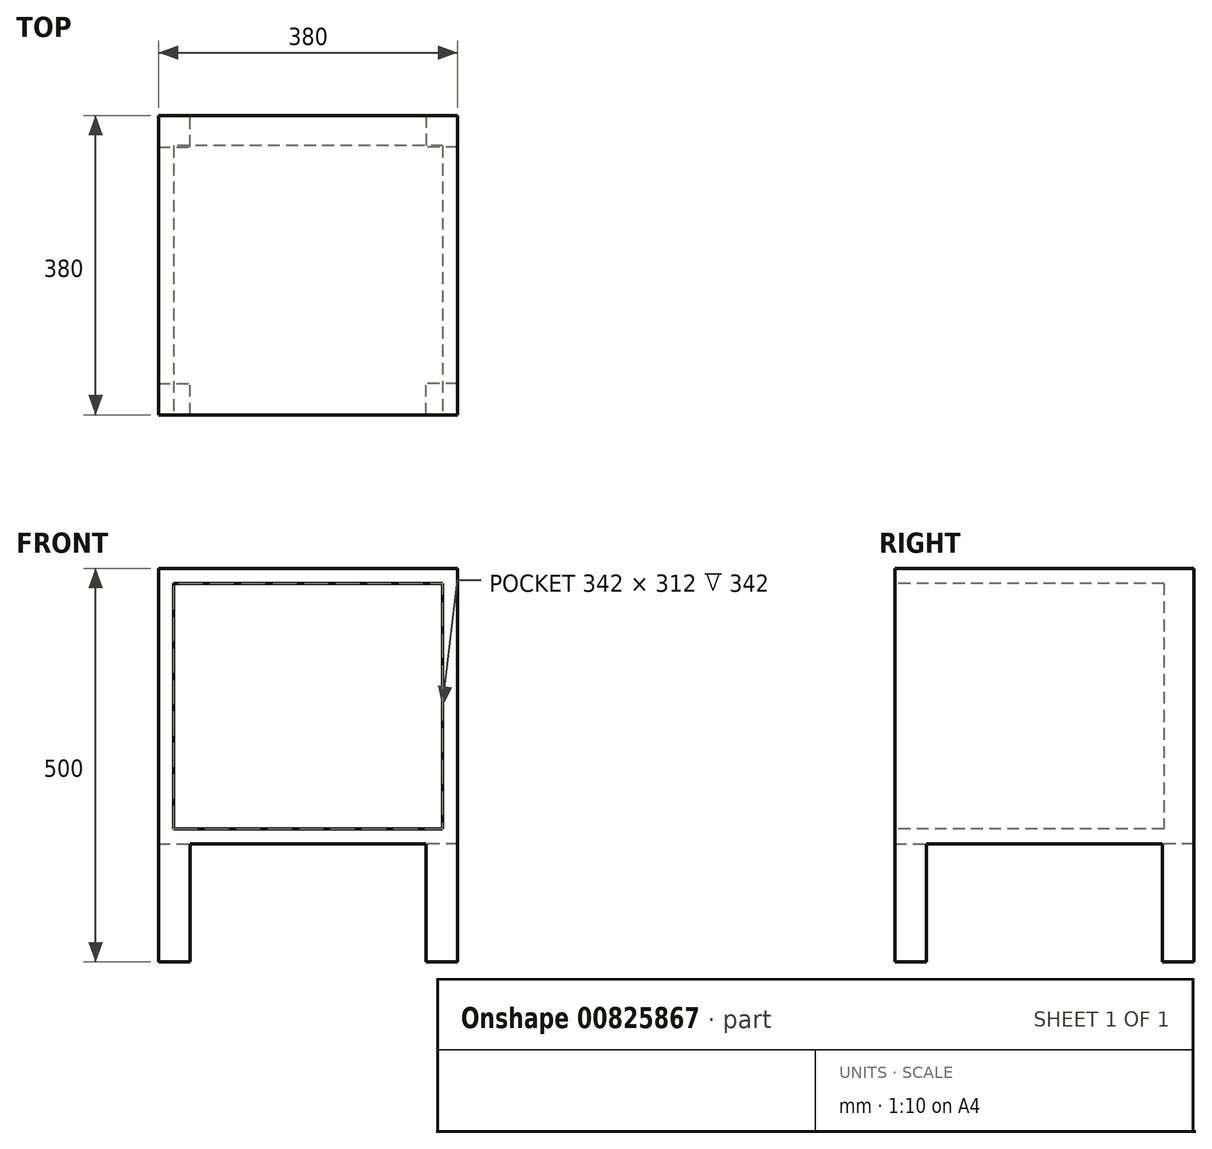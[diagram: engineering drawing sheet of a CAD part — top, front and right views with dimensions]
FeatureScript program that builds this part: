
annotation { "Feature Type Name" : "Feature", "Feature Type Description" : "" }
export const myFeature = defineFeature(function(context is Context, id is Id, definition is map)
    precondition{}
    {
        {
            var Q0;
            Q0=qCreatedBy(makeId("Top.planeOp"),FACE);
            var sketch = newSketch(context, id + "F0", { "sketchPlane" : qUnion([Q0])});
            skLineSegment(sketch, "E0.bottom", {"start": v(-190, 190) * mm, "end": v(190, 190) * mm});
            skLineSegment(sketch, "E0.top", {"start": v(-190, -190) * mm, "end": v(190, -190) * mm});
            skLineSegment(sketch, "E0.left", {"start": v(-190, 190) * mm, "end": v(-190, -190) * mm});
            skLineSegment(sketch, "E0.right", {"start": v(190, 190) * mm, "end": v(190, -190) * mm});
            skPoint(sketch, "E0.middle", {"position": v(0, 0) * mm});
            skSolve(sketch);
        }
        {
            var Q0;
            Q0 = qSketchRegion(id + "F0", true);
            extrude(context, id + "F1", {"entities" : qUnion([Q0]), "depth" : 350 * mm, "offsetDistance" : 25 * mm});
        }
        {
            var Q0;
            Q0=makeQuery(id+"F1.opExtrude","SWEPT_FACE",FACE,{"disambiguationData":[OSD([sQuery(id+"F0.wireOp",EDGE,"E0.top")])]});
            var sketch = newSketch(context, id + "F2", { "sketchPlane" : qUnion([Q0])});
            skLineSegment(sketch, "E1.bottom", {"start": v(171, 331) * mm, "end": v(-171, 331) * mm});
            skLineSegment(sketch, "E1.top", {"start": v(171, 19) * mm, "end": v(-171, 19) * mm});
            skLineSegment(sketch, "E1.left", {"start": v(171, 331) * mm, "end": v(171, 19) * mm});
            skLineSegment(sketch, "E1.right", {"start": v(-171, 331) * mm, "end": v(-171, 19) * mm});
            skPoint(sketch, "E1.middle", {"position": v(0, 175) * mm});
            skPoint(sketch, "E1.middle.positionSnap0", {"position": v(190, 175) * mm});
            skPoint(sketch, "E1.middle.positionSnap1", {"position": v(0, 0) * mm});
            skPoint(sketch, "E1.centerSnap0", {"position": v(190, 175) * mm});
            skPoint(sketch, "E1.centerSnap1", {"position": v(0, 0) * mm});
            skSolve(sketch);
        }
        {
            var Q0;
            Q0=makeQuery(id+"F2.imprint","IMPRINT",FACE,{"disambiguationData":[TD([[makeQuery(id+"F2.imprint","IMPRINT",EDGE,{"derivedFrom":sQuery(id+"F2.wireOp",EDGE,"E1.bottom")}),1.0]])]});
            extrude(context, id + "F3", {"entities" : qUnion([Q0]), "operationType" : NewBodyOperationType.REMOVE, "oppositeDirection" : true, "depth" : 342 * mm, "offsetDistance" : 25 * mm});
        }
        {
            var Q0;
            Q0=makeQuery(id+"F1.opExtrude","CAP_FACE",FACE,{"disambiguationData":[OSD([sQuery(id+"F0.wireOp",EDGE,"E0.bottom"),sQuery(id+"F0.wireOp",EDGE,"E0.top"),sQuery(id+"F0.wireOp",EDGE,"E0.left"),sQuery(id+"F0.wireOp",EDGE,"E0.right")])],"isStart":true});
            var sketch = newSketch(context, id + "F4", { "sketchPlane" : qUnion([Q0])});
            skLineSegment(sketch, "E2.bottom", {"start": v(-190, 190) * mm, "end": v(-150, 190) * mm});
            skLineSegment(sketch, "E2.top", {"start": v(-190, 150) * mm, "end": v(-150, 150) * mm});
            skLineSegment(sketch, "E2.left", {"start": v(-190, 190) * mm, "end": v(-190, 150) * mm});
            skLineSegment(sketch, "E2.right", {"start": v(-150, 190) * mm, "end": v(-150, 150) * mm});
            skLineSegment(sketch, "E3.bottom", {"start": v(190, 190) * mm, "end": v(150, 190) * mm});
            skLineSegment(sketch, "E3.top", {"start": v(190, 150) * mm, "end": v(150, 150) * mm});
            skLineSegment(sketch, "E3.left", {"start": v(190, 190) * mm, "end": v(190, 150) * mm});
            skLineSegment(sketch, "E3.right", {"start": v(150, 190) * mm, "end": v(150, 150) * mm});
            skLineSegment(sketch, "E4.bottom", {"start": v(-190, -150) * mm, "end": v(-150, -150) * mm});
            skLineSegment(sketch, "E4.top", {"start": v(-190, -190) * mm, "end": v(-150, -190) * mm});
            skLineSegment(sketch, "E4.left", {"start": v(-190, -150) * mm, "end": v(-190, -190) * mm});
            skLineSegment(sketch, "E4.right", {"start": v(-150, -150) * mm, "end": v(-150, -190) * mm});
            skLineSegment(sketch, "E5.bottom", {"start": v(190, -190) * mm, "end": v(150, -190) * mm});
            skLineSegment(sketch, "E5.top", {"start": v(190, -150) * mm, "end": v(150, -150) * mm});
            skLineSegment(sketch, "E5.left", {"start": v(190, -190) * mm, "end": v(190, -150) * mm});
            skLineSegment(sketch, "E5.right", {"start": v(150, -190) * mm, "end": v(150, -150) * mm});
            skSolve(sketch);
        }
        {
            var Q0;
            Q0=makeQuery(id+"F4.imprint","IMPRINT",FACE,{"disambiguationData":[TD([[makeQuery(id+"F4.imprint","IMPRINT",EDGE,{"derivedFrom":sQuery(id+"F4.wireOp",EDGE,"E2.bottom")}),-1.0]])]});
            var Q1;
            Q1=makeQuery(id+"F4.imprint","IMPRINT",FACE,{"disambiguationData":[TD([[makeQuery(id+"F4.imprint","IMPRINT",EDGE,{"derivedFrom":sQuery(id+"F4.wireOp",EDGE,"E3.bottom")}),-1.0]])]});
            var Q2;
            Q2=makeQuery(id+"F4.imprint","IMPRINT",FACE,{"disambiguationData":[TD([[makeQuery(id+"F4.imprint","IMPRINT",EDGE,{"derivedFrom":sQuery(id+"F4.wireOp",EDGE,"E5.bottom")}),1.0]])]});
            var Q3;
            Q3=makeQuery(id+"F4.imprint","IMPRINT",FACE,{"disambiguationData":[TD([[makeQuery(id+"F4.imprint","IMPRINT",EDGE,{"derivedFrom":sQuery(id+"F4.wireOp",EDGE,"E4.bottom")}),-1.0]])]});
            extrude(context, id + "F5", {"entities" : qUnion([Q0, Q1, Q2, Q3]), "operationType" : NewBodyOperationType.ADD, "depth" : 150 * mm, "offsetDistance" : 25 * mm});
        }
    });
